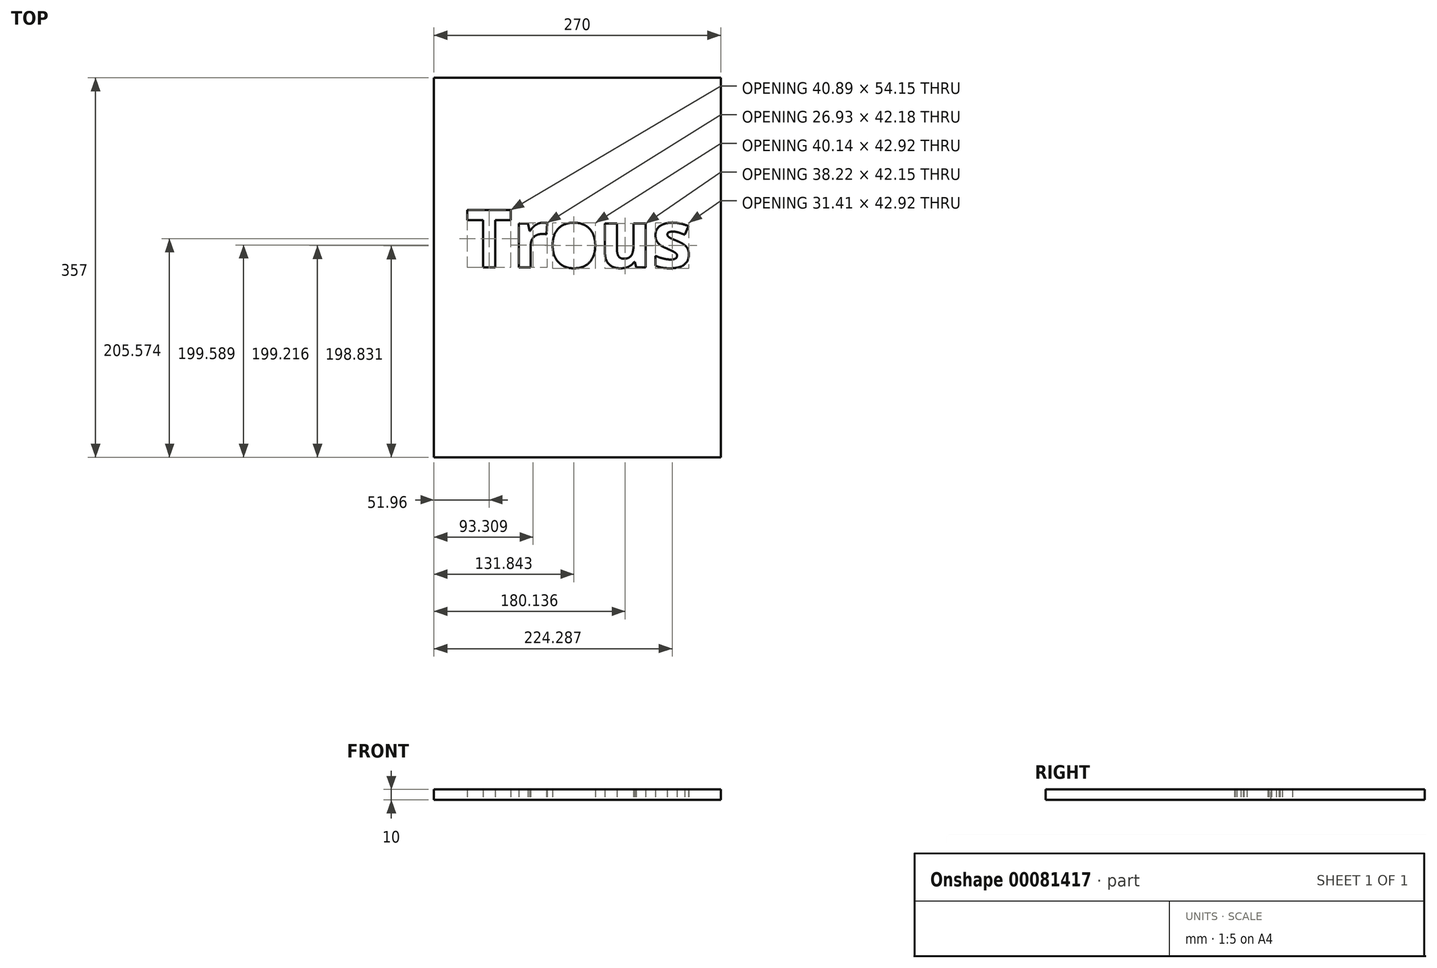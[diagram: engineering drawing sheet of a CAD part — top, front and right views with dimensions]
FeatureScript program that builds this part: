
annotation { "Feature Type Name" : "Feature", "Feature Type Description" : "" }
export const myFeature = defineFeature(function(context is Context, id is Id, definition is map)
    precondition{}
    {
        {
            var Q0;
            Q0=qCreatedBy(makeId("Top.planeOp"),FACE);
            var sketch = newSketch(context, id + "F0", { "sketchPlane" : qUnion([Q0])});
            skLineSegment(sketch, "E0.bottom", {"start": v(-135, -211.68) * mm, "end": v(135, -211.68) * mm});
            skLineSegment(sketch, "E0.top", {"start": v(-135, 145.32) * mm, "end": v(135, 145.32) * mm});
            skLineSegment(sketch, "E0.left", {"start": v(-135, -211.68) * mm, "end": v(-135, 145.32) * mm});
            skLineSegment(sketch, "E0.right", {"start": v(135, -211.68) * mm, "end": v(135, 145.32) * mm});
            skLineSegment(sketch, "E1.bottom", {"start": v(-105, 115.32) * mm, "end": v(105, 115.32) * mm});
            skLineSegment(sketch, "E1.top", {"start": v(-105, -181.68) * mm, "end": v(105, -181.68) * mm});
            skLineSegment(sketch, "E1.left", {"start": v(-105, 115.32) * mm, "end": v(-105, -181.68) * mm});
            skLineSegment(sketch, "E1.right", {"start": v(105, 115.32) * mm, "end": v(105, -181.68) * mm});
            skLineSegment(sketch, "E2", {"start": v(0, 145.32) * mm, "end": v(0, 115.32) * mm});
            skPoint(sketch, "E2.startSnap0", {"position": v(0, 115.32) * mm});
            skPoint(sketch, "E2.endSnap0", {"position": v(0, 115.32) * mm});
            skLineSegment(sketch, "E3", {"start": v(135, -33.18) * mm, "end": v(105, -33.18) * mm});
            skPoint(sketch, "E3.endSnap0", {"position": v(105, -33.18) * mm});
            skLineSegment(sketch, "E4", {"start": v(81.15, -211.68) * mm, "end": v(81.15, -181.68) * mm});
            skLineSegment(sketch, "E5", {"start": v(-135, -111.87) * mm, "end": v(-105, -111.87) * mm});
            skText(sketch, "E6", { "text": "Trous", "fontName": "OpenSans-Bold.ttf"});
            const initialGuessF0  = {"E6": [-0.105, -0.03318, 1, 0, 0.05461]};
            skSetInitialGuess(sketch, initialGuessF0);
            skSolve(sketch);
        }
        {
            var Q0;
            {var subQ7=sQuery(id+"F0.wireOp",EDGE,"E2");Q0=makeQuery(id+"F0.imprint","IMPRINT",FACE,{"disambiguationData":[TD([[makeQuery(id+"F0.imprint","IMPRINT",EDGE,{"derivedFrom":subQ7}),-1.0]])]});}
            var Q1;
            {var subQ3=sQuery(id+"F0.wireOp",EDGE,"E3");Q1=makeQuery(id+"F0.imprint","IMPRINT",FACE,{"disambiguationData":[TD([[makeQuery(id+"F0.imprint","IMPRINT",EDGE,{"derivedFrom":subQ3}),1.0]])]});}
            var Q2;
            {var subQ7=sQuery(id+"F0.wireOp",EDGE,"E2");Q2=makeQuery(id+"F0.imprint","IMPRINT",FACE,{"disambiguationData":[TD([[makeQuery(id+"F0.imprint","IMPRINT",EDGE,{"derivedFrom":subQ7}),1.0]])]});}
            var Q3;
            {var subQ4=sQuery(id+"F0.wireOp",EDGE,"E4");Q3=makeQuery(id+"F0.imprint","IMPRINT",FACE,{"disambiguationData":[TD([[makeQuery(id+"F0.imprint","IMPRINT",EDGE,{"derivedFrom":subQ4}),1.0]])]});}
            var Q4;
            Q4=makeQuery(id+"F0.imprint","IMPRINT",FACE,{"disambiguationData":[TD([[makeQuery(id+"F0.imprint","IMPRINT",EDGE,{"derivedFrom":sQuery(id+"F0.wireOp",EDGE,"0i8niirV-KoD6-kgjG-p0xN-2Ku66xTdw6wE")}),-1.0]])]});
            var Q5;
            Q5=makeQuery(id+"F0.imprint","IMPRINT",FACE,{"disambiguationData":[TD([[makeQuery(id+"F0.imprint","IMPRINT",EDGE,{"derivedFrom":sQuery(id+"F0.wireOp",EDGE,"E6.sketch_text.stroke-0")}),1.0]])]});
            extrude(context, id + "F1", {"entities" : qUnion([Q0, Q1, Q2, Q3, Q4, Q5]), "depth" : 10 * mm});
        }
    });
